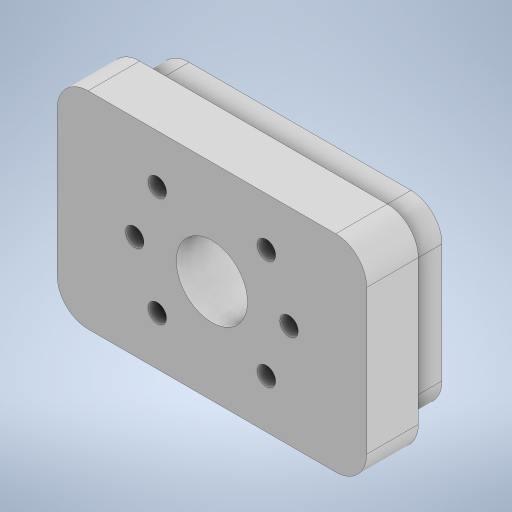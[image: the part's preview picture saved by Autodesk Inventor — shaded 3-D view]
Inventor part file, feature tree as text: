
AUTODESK INVENTOR PART (.ipt)
format: ipt  version: 2023 (Build 270158000, 158)  size: 294,400 bytes
history: native  units: in
note: dims shown in document units (in); Inventor stores cm internally (conversion verified against a paired STEP export)
features: sketch x5, extrude x3, fillet x2, projected_geometry x2, chamfer x1, plane x1
ambient origin geometry x8: Origin, YZ Plane, XZ Plane, XY Plane, X Axis, Y Axis, Z Axis, Center Point
bodies: Solid1 (feature_tree)
feature tree (14):
  extrude  "Extrusion1"  Depth=1.75in
  extrude  "Extrusion2"  Depth=0.3543in TaperAngle=0.0deg
  fillet  "Fillet1"  Radius=3.0in
  extrude  "Extrusion3"  Depth=0.3in
  chamfer  "Chamfer1"  Distance=0.5in
  sketch  "Sketch4"  dims[d11=0.689in]
  plane  "Work Plane1"
  sketch  "Sketch8"  dims[d12=0.5in d13=0.0in d14=0.1772in d15=1.4961in d16=45.0deg d17=0.05in d18=0.125in d19=45.0deg d30=0.025in]
  fillet  "Fillet2"  Radius=0.125in
  sketch  "Sketch1"  dims[d0=2.75in d1=1.75in]
  sketch  "Sketch2"  dims[d2=0.3in d3=0.3543in d4=0.0in d5=3.0in]
  sketch  "Sketch3"  dims[d6=2.0in d7=0.3in d8=0.5in d9=0.0in d10=0.125in]
  projected_geometry  "Projected Loop1"
  projected_geometry  "Projected Loop2"
